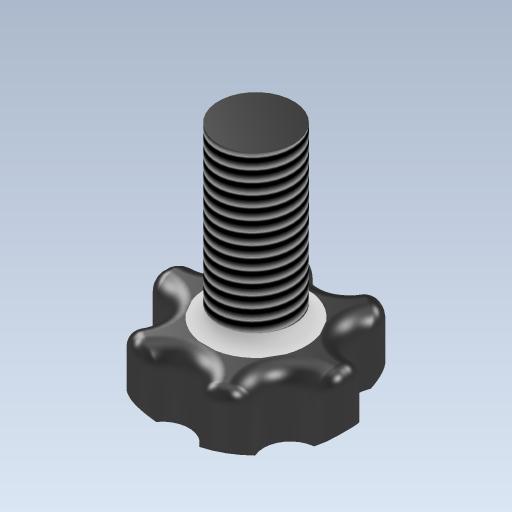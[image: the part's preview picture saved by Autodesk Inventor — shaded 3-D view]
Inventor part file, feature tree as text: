
AUTODESK INVENTOR PART (.ipt)
format: ipt  version: 2023 (Build 270158030, 158C)  size: 434,688 bytes
history: native  units: mm
features: other x4, fillet x1
ambient origin geometry x8: Origin, YZ Plane, XZ Plane, XY Plane, X Axis, Y Axis, Z Axis, Center Point
bodies: Body1 (feature_tree)
feature tree (5):
  other  "pigion-bath.ipt"
  fillet  "Fillet1"  Radius=10.0mm
  other  "screw::pigion-bath.ipt"
  other  "TaggingFeature1"
  other  "screw"
